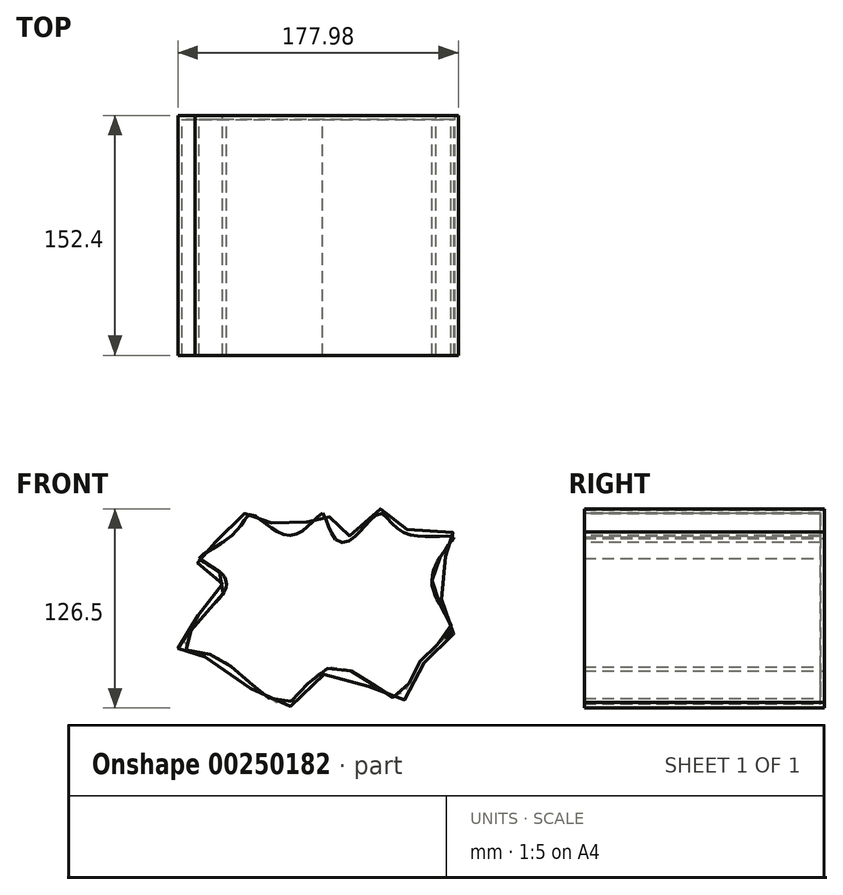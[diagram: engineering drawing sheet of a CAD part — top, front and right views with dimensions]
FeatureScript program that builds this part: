
annotation { "Feature Type Name" : "Feature", "Feature Type Description" : "" }
export const myFeature = defineFeature(function(context is Context, id is Id, definition is map)
    precondition{}
    {
        {
            var Q0;
            Q0=qCreatedBy(makeId("Front.planeOp"),FACE);
            var sketch = newSketch(context, id + "F0", { "sketchPlane" : qUnion([Q0])});
            skFitSpline(sketch, "E0", {"points": [v(-72.68, 8.22) * mm, v(-57.79, 30.9) * mm, v(-74.45, 44) * mm, v(-52, 61.79) * mm, v(-38.67, 75.12) * mm, v(-12.9, 61.79) * mm, v(7.33, 75.79) * mm, v(18.45, 57.12) * mm, v(42.23, 75.79) * mm, v(59.34, 63.12) * mm, v(92.46, 59.56) * mm, v(78.45, 32) * mm, v(90.68, 0) * mm, v(69.79, -23.34) * mm, v(54.9, -47.12) * mm, v(13.34, -27.11) * mm, v(-17.11, -50.45) * mm, v(-61.79, -20.45) * mm, v(-84.9, -14) * mm, v(-72.68, 8.22) * mm]});
            skSolve(sketch);
        }
        {
            var Q0;
            Q0=makeQuery(id+"F0.imprint","IMPRINT",FACE,{"disambiguationData":[TD([[makeQuery(id+"F0.imprint","IMPRINT",EDGE,{"derivedFrom":sQuery(id+"F0.wireOp",EDGE,"E0")}),-1.0]])]});
            extrude(context, id + "F1", {"entities" : qUnion([Q0]), "depth" : 152.4 * mm});
        }
        {
            var Q0;
            Q0=makeQuery(id+"F1.opExtrude","CAP_FACE",FACE,{"disambiguationData":[OSD([sQuery(id+"F0.wireOp",EDGE,"E0")])],"isStart":false});
            shell(context, id + "F2", {"entities" : qUnion([Q0]), "thickness" : 2.54 * mm});
        }
    });
